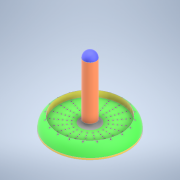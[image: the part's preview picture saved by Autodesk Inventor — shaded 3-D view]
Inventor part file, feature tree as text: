
AUTODESK INVENTOR PART (.ipt)
format: ipt  version: 2021 (Build 250183000, 183)  size: 392,192 bytes
history: native  units: mm
features: extrude x4, sketch x4, fillet x3, pattern_circular x2, shell x1
ambient origin geometry x8: Origin, YZ Plane, XZ Plane, XY Plane, X Axis, Y Axis, Z Axis, Center Point
bodies: Solid1 (feature_tree)
feature tree (14):
  extrude  "Extrusion1"  Depth=2.0mm TaperAngle=0.0deg
  shell  "Shell1"  Thickness=1.0mm
  fillet  "Fillet1"  Radius=2.0mm
  extrude  "Extrusion2"  Depth=10.0mm TaperAngle=0.0deg
  fillet  "Fillet2"  Radius=1.0mm
  fillet  "Fillet3"  Radius=0.5mm
  extrude  "Extrusion3"  Depth=2.1mm
  pattern_circular  "Circular Pattern1"  Count=20 Angle=360.0deg
  extrude  "Extrusion4"  Depth=10.0mm
  pattern_circular  "Circular Pattern2"  Count=6  [1 undecoded]
  sketch  "Sketch1"  dims[d0=12.0mm d1=2.0mm d2=0.0mm d3=1.0mm d4=2.0mm]
  sketch  "Sketch2"  dims[d5=2.0mm d6=10.0mm d7=0.0mm d8=1.0mm d9=0.5mm]
  sketch  "Sketch3"  dims[d10=0.2mm d11=2.1mm]
  sketch  "Sketch4"  dims[d12=10.0mm d13=0.0mm d14=200.0mm d15=360.0deg d17=0.2mm d18=60.0mm d20=0.5mm d21=10.0mm d23=10.0mm d25=10.0mm d26=0.0mm d27=200.0mm d28=360.0deg]
note: 1 required parameter value undecoded (feature->parameter linkage not recoverable at this tier; creation-order binding heuristic only, values carry confidence <= 0.55)
